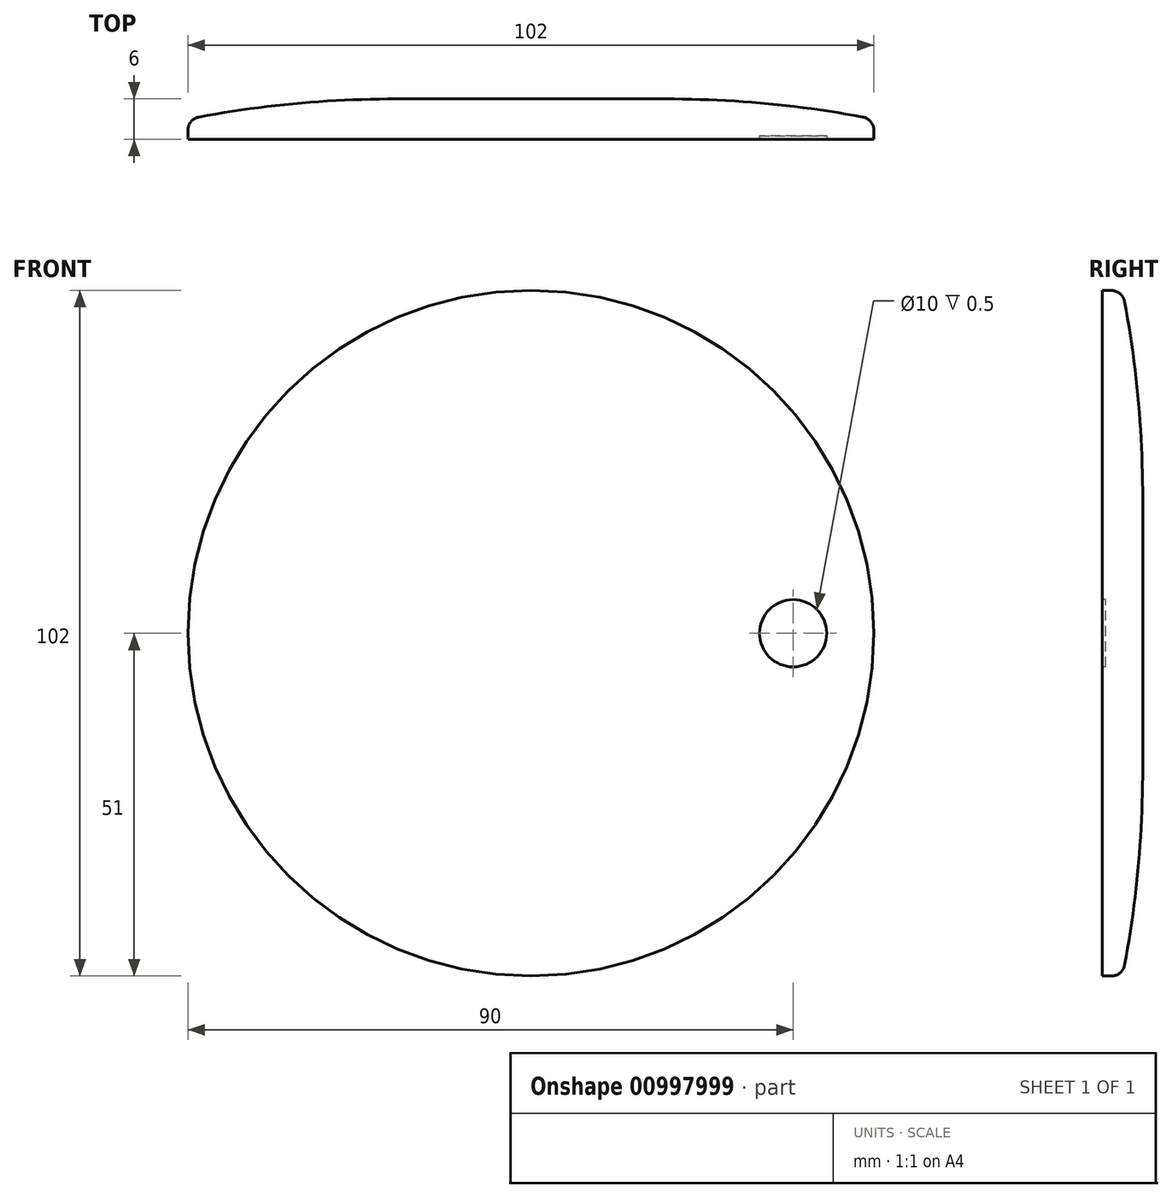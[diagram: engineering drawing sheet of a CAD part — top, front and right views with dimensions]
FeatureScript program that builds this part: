
annotation { "Feature Type Name" : "Feature", "Feature Type Description" : "" }
export const myFeature = defineFeature(function(context is Context, id is Id, definition is map)
    precondition{}
    {
        {
            var Q0;
            Q0=qCreatedBy(makeId("Top.planeOp"),FACE);
            var sketch = newSketch(context, id + "F0", { "sketchPlane" : qUnion([Q0])});
            skLineSegment(sketch, "E0", {"start": v(0, 0) * mm, "end": v(0, 6) * mm});
            skLineSegment(sketch, "E1", {"start": v(0, 6) * mm, "end": v(20, 6) * mm});
            skLineSegment(sketch, "E2", {"start": v(0, 0) * mm, "end": v(51, 0) * mm});
            skLineSegment(sketch, "E3", {"start": v(51, 0) * mm, "end": v(51, 1.34) * mm});
            skArc(sketch, "E4", {"start": v(20, 6) * mm, "mid": v(34.74, 5.33) * mm, "end": v(49.36, 3.31) * mm});
            skPoint(sketch, "E5.visualSharp", {"position": v(51, 3) * mm});
            skArc(sketch, "E5.filletArc", {"start": v(51, 1.34) * mm, "mid": v(50.54, 2.62) * mm, "end": v(49.36, 3.31) * mm});
            skSolve(sketch);
        }
        {
            var Q0;
            Q0 = qSketchRegion(id + "F0", true);
            var Q1;
            Q1=sQuery(id+"F0.wireOp",EDGE,"E0");
            revolve(context, id + "F1", {"surfaceOperationType" : NewSurfaceOperationType.NEW, "entities" : qUnion([Q0]), "axis" : qUnion([Q1]), "revolveType" : RevolveType.FULL});
        }
        {
            var Q0;
            Q0=makeQuery(id+"F1.opRevolve","SWEPT_FACE",FACE,{"disambiguationData":[OSD([sQuery(id+"F0.wireOp",EDGE,"E2")])]});
            var sketch = newSketch(context, id + "F2", { "sketchPlane" : qUnion([Q0])});
            skLineSegment(sketch, "E6", {"start": v(0, 0) * mm, "end": v(39, 0) * mm, "construction": true});
            skCircle(sketch, "E7", {"center": v(39, 0) * mm, "radius": 5 * mm});
            skSolve(sketch);
        }
        {
            var Q0;
            Q0=makeQuery(id+"F2.imprint","IMPRINT",FACE,{"disambiguationData":[TD([[makeQuery(id+"F2.imprint","IMPRINT",EDGE,{"derivedFrom":sQuery(id+"F2.wireOp",EDGE,"E7")}),1.0]])]});
            extrude(context, id + "F3", {"entities" : qUnion([Q0]), "operationType" : NewBodyOperationType.REMOVE, "oppositeDirection" : true, "depth" : 0.5 * mm, "offsetDistance" : 25 * mm});
        }
        {
            var Q0;
            Q0=qCreatedBy(makeId("Top.planeOp"),FACE);
            var sketch = newSketch(context, id + "F4", { "sketchPlane" : qUnion([Q0])});
            skLineSegment(sketch, "E8", {"start": v(0, 0) * mm, "end": v(0, -55) * mm, "construction": true});
            skSolve(sketch);
        }
    });
